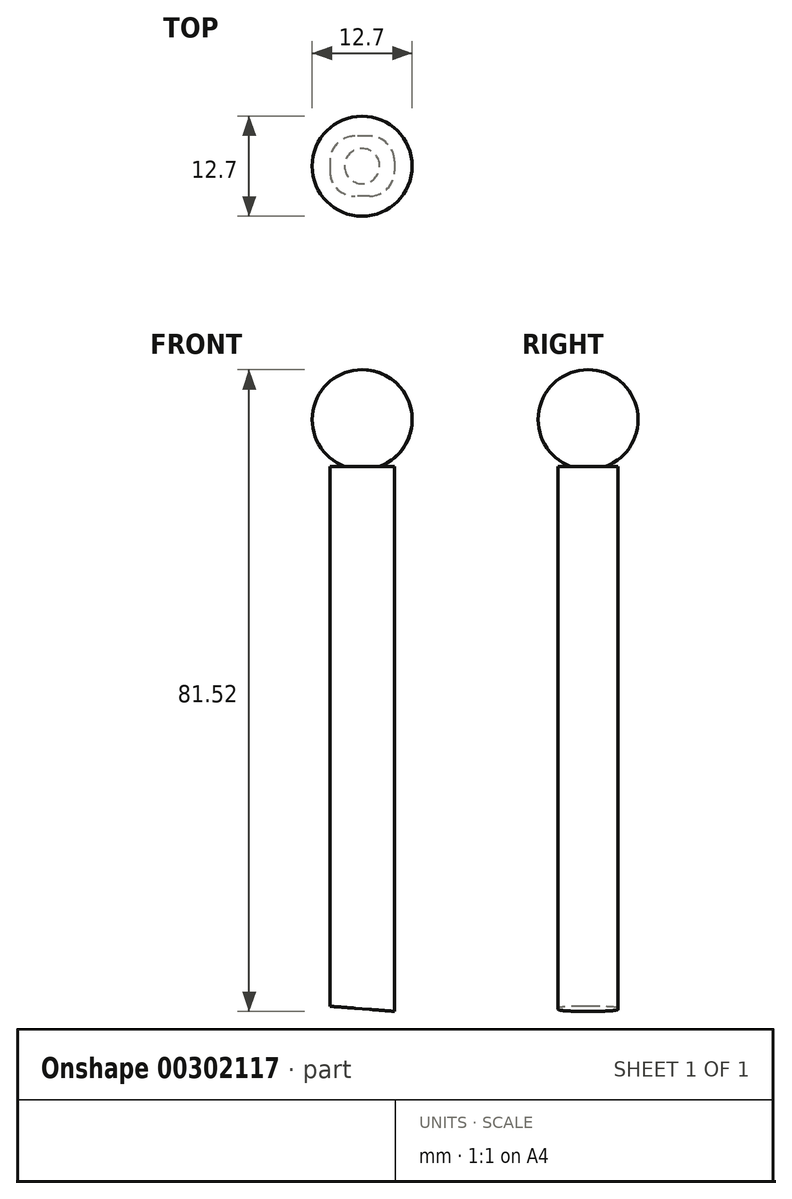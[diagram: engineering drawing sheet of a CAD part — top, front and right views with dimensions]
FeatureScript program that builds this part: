
annotation { "Feature Type Name" : "Feature", "Feature Type Description" : "" }
export const myFeature = defineFeature(function(context is Context, id is Id, definition is map)
    precondition{}
    {
        {
            var Q0;
            Q0=qCreatedBy(makeId("Front.planeOp"),FACE);
            var sketch = newSketch(context, id + "F0", { "sketchPlane" : qUnion([Q0])});
            skCircle(sketch, "E0", {"center": v(0, 0) * mm, "radius": 6.35 * mm});
            skLineSegment(sketch, "E1", {"start": v(0, 6.35) * mm, "end": v(0, -6.35) * mm});
            skSolve(sketch);
        }
        {
            var Q0;
            {var subQ0=sQuery(id+"F0.wireOp",EDGE,"E1");Q0=makeQuery(id+"F0.imprint","IMPRINT",FACE,{"disambiguationData":[TD([[makeQuery(id+"F0.imprint","IMPRINT",EDGE,{"derivedFrom":subQ0}),-1.0]])]});}
            var Q1;
            Q1=sQuery(id+"F0.wireOp",EDGE,"E1");
            revolve(context, id + "F1", {"entities" : qUnion([Q0]), "axis" : qUnion([Q1]), "revolveType" : RevolveType.FULL});
        }
        {
            var Q0;
            Q0=qCreatedBy(makeId("Front.planeOp"),FACE);
            var sketch = newSketch(context, id + "F2", { "sketchPlane" : qUnion([Q0])});
            skLineSegment(sketch, "E2", {"start": v(-4.11, -5.94) * mm, "end": v(-4.11, -74.52) * mm});
            skLineSegment(sketch, "E3", {"start": v(4.11, -5.94) * mm, "end": v(4.11, -75.17) * mm});
            skLineSegment(sketch, "E4", {"start": v(4.11, -75.17) * mm, "end": v(-4.11, -74.52) * mm});
            skLineSegment(sketch, "E5", {"start": v(-4.11, -5.94) * mm, "end": v(4.11, -5.94) * mm});
            skSolve(sketch);
        }
        {
            var Q0;
            Q0=makeQuery(id+"F2.imprint","IMPRINT",FACE,{"disambiguationData":[TD([[makeQuery(id+"F2.imprint","IMPRINT",EDGE,{"derivedFrom":sQuery(id+"F2.wireOp",EDGE,"E2")}),1.0]])]});
            extrude(context, id + "F3", {"entities" : qUnion([Q0]), "operationType" : NewBodyOperationType.ADD, "oppositeDirection" : true, "depth" : 3.8 * mm, "hasSecondDirection" : true, "secondDirectionOppositeDirection" : false, "secondDirectionDepth" : 3.8 * mm});
        }
        {
            var Q0;
            Q0=makeQuery(id+"F3.opExtrude","CAP_EDGE",EDGE,{"disambiguationData":[OSD([sQuery(id+"F2.wireOp",EDGE,"E3")])],"isStart":true});
            var Q1;
            Q1=makeQuery(id+"F3.opExtrude","CAP_EDGE",EDGE,{"disambiguationData":[OSD([sQuery(id+"F2.wireOp",EDGE,"E3")])],"isStart":false});
            var Q2;
            Q2=makeQuery(id+"F3.opExtrude","CAP_EDGE",EDGE,{"disambiguationData":[OSD([sQuery(id+"F2.wireOp",EDGE,"E2")])],"isStart":true});
            var Q3;
            Q3=makeQuery(id+"F3.opExtrude","CAP_EDGE",EDGE,{"disambiguationData":[OSD([sQuery(id+"F2.wireOp",EDGE,"E2")])],"isStart":false});
            fillet(context, id + "F4", {"entities" : qUnion([Q0, Q1, Q2, Q3]), "radius" : 3.17 * mm, "tangentPropagation" : true, "allowEdgeOverflow" : false});
        }
    });
